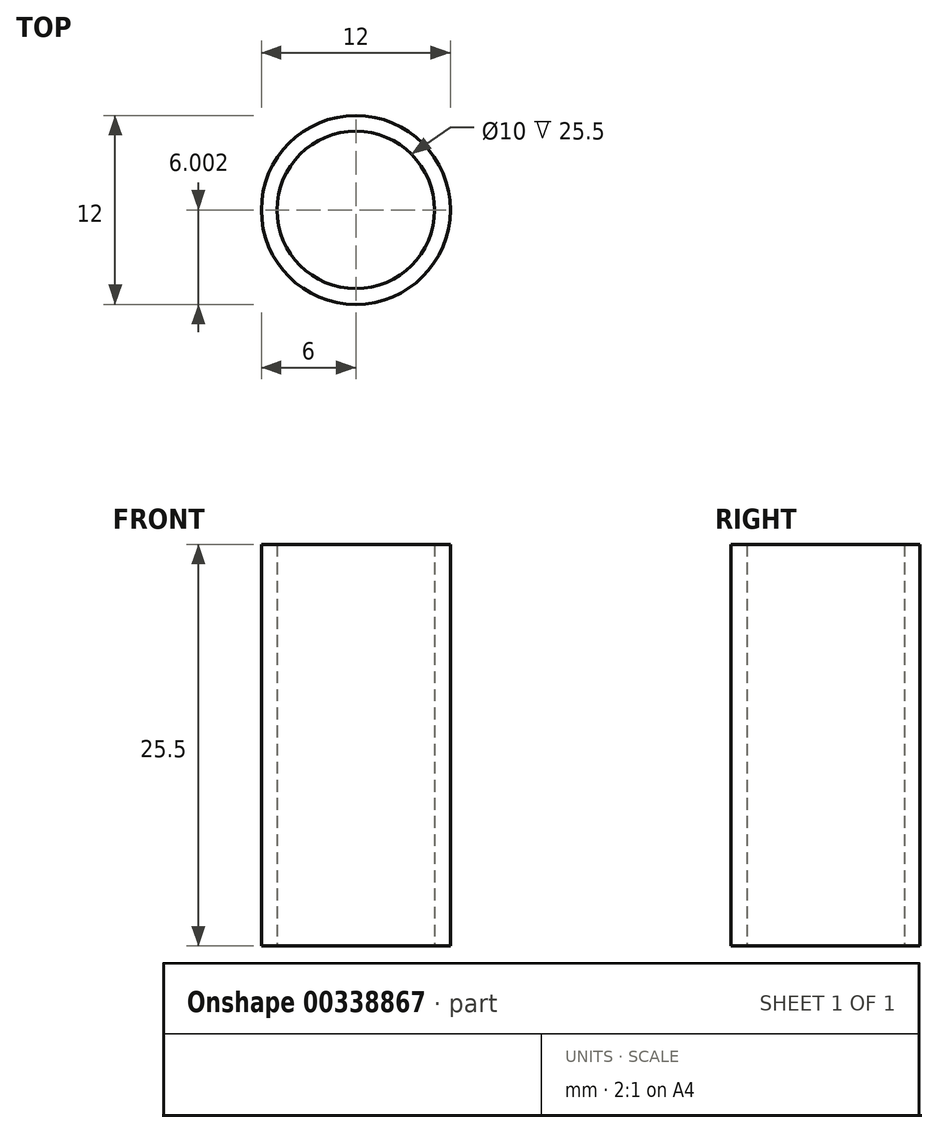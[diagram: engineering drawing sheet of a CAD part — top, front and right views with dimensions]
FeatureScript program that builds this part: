
annotation { "Feature Type Name" : "Feature", "Feature Type Description" : "" }
export const myFeature = defineFeature(function(context is Context, id is Id, definition is map)
    precondition{}
    {
        {
            var Q0;
            Q0=qCreatedBy(makeId("Top.planeOp"),FACE);
            var sketch = newSketch(context, id + "F0", { "sketchPlane" : qUnion([Q0])});
            skCircle(sketch, "E0", {"center": v(0, -2.37) * mm, "radius": 6 * mm});
            skCircle(sketch, "E1", {"center": v(0, -2.37) * mm, "radius": 5 * mm});
            skSolve(sketch);
        }
        {
            var Q0;
            Q0 = qSketchRegion(id + "F0", true);
            extrude(context, id + "F1", {"entities" : qUnion([Q0]), "depth" : 25.5 * mm});
        }
    });
